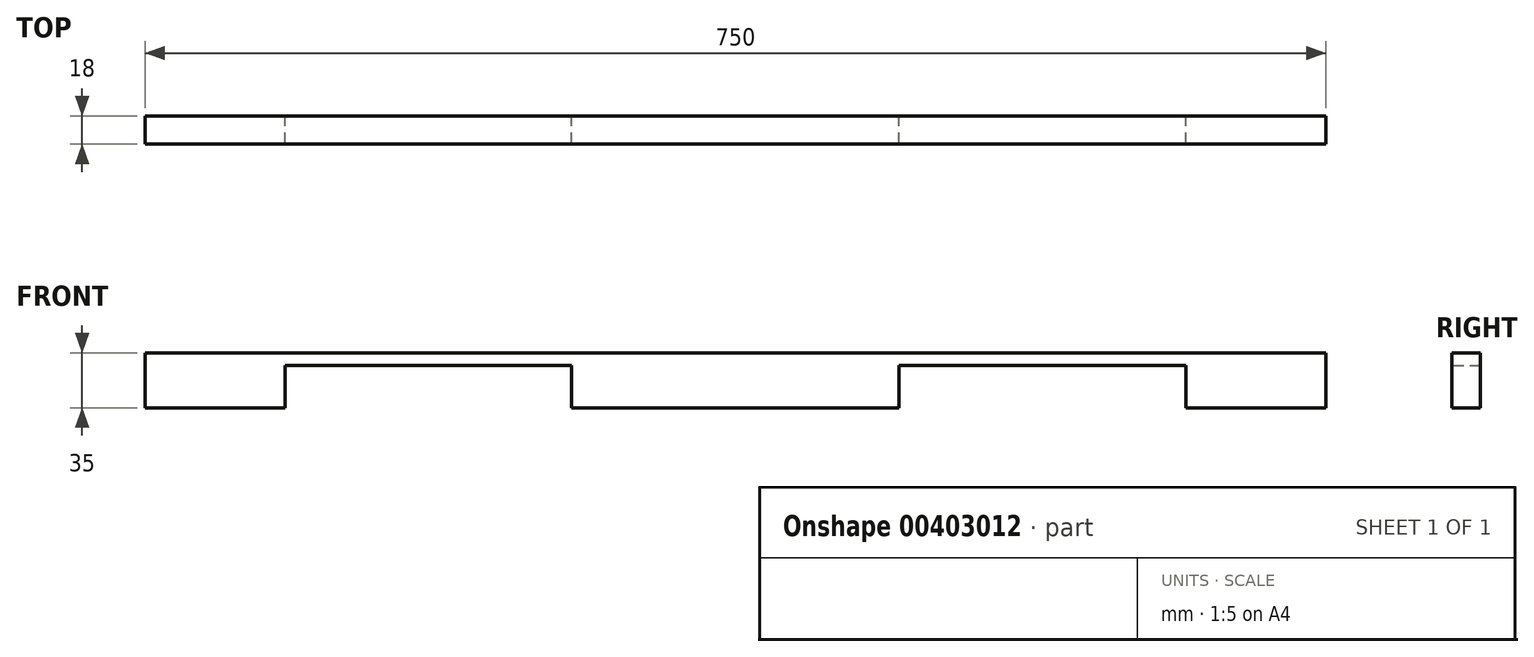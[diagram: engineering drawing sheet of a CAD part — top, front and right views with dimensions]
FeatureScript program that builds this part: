
annotation { "Feature Type Name" : "Feature", "Feature Type Description" : "" }
export const myFeature = defineFeature(function(context is Context, id is Id, definition is map)
    precondition{}
    {
        {
            var Q0;
            Q0=qCreatedBy(makeId("Front.planeOp"),FACE);
            var sketch = newSketch(context, id + "F0", { "sketchPlane" : qUnion([Q0])});
            skLineSegment(sketch, "E0.bottom", {"start": v(0, 0) * mm, "end": v(89, 0) * mm});
            skLineSegment(sketch, "E0.left", {"start": v(0, 0) * mm, "end": v(0, 35) * mm});
            skLineSegment(sketch, "E0.right", {"start": v(750, 0) * mm, "end": v(750, 35) * mm});
            skLineSegment(sketch, "E1.top", {"start": v(89, 27) * mm, "end": v(271, 27) * mm});
            skLineSegment(sketch, "E1.left", {"start": v(89, 0) * mm, "end": v(89, 27) * mm});
            skLineSegment(sketch, "E1.right", {"start": v(271, 0) * mm, "end": v(271, 27) * mm});
            skLineSegment(sketch, "E2.top", {"start": v(479, 27) * mm, "end": v(661, 27) * mm});
            skLineSegment(sketch, "E2.left", {"start": v(479, 0) * mm, "end": v(479, 27) * mm});
            skLineSegment(sketch, "E2.right", {"start": v(661, 0) * mm, "end": v(661, 27) * mm});
            skLineSegment(sketch, "E3.trimOffspring", {"start": v(271, 0) * mm, "end": v(479, 0) * mm});
            skLineSegment(sketch, "E4.trimOffspring", {"start": v(661, 0) * mm, "end": v(750, 0) * mm});
            skLineSegment(sketch, "E5", {"start": v(0, 35) * mm, "end": v(750, 35) * mm});
            skSolve(sketch);
        }
        {
            var Q0;
            Q0=makeQuery(id+"F0.imprint","IMPRINT",FACE,{"disambiguationData":[TD([[makeQuery(id+"F0.imprint","IMPRINT",EDGE,{"derivedFrom":sQuery(id+"F0.wireOp",EDGE,"E0.bottom")}),1.0]])]});
            extrude(context, id + "F1", {"entities" : qUnion([Q0]), "depth" : 18 * mm});
        }
    });
